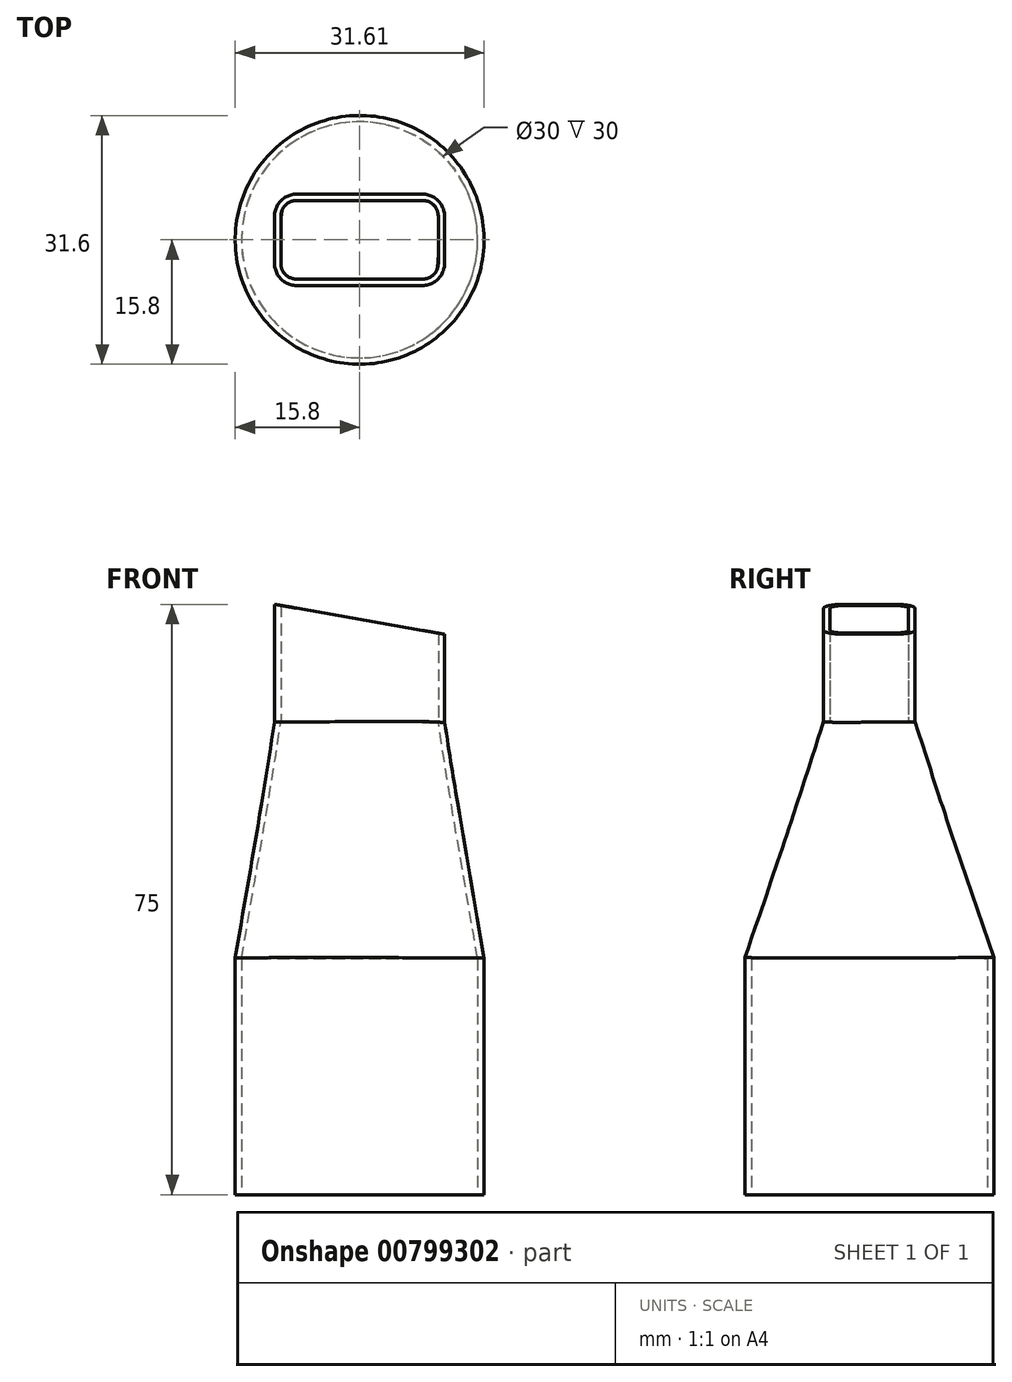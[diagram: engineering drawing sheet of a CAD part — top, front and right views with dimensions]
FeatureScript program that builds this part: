
annotation { "Feature Type Name" : "Feature", "Feature Type Description" : "" }
export const myFeature = defineFeature(function(context is Context, id is Id, definition is map)
    precondition{}
    {
        {
            var Q0;
            Q0=qCreatedBy(makeId("Top.planeOp"),FACE);
            var sketch = newSketch(context, id + "F0", { "sketchPlane" : qUnion([Q0])});
            skCircle(sketch, "E0", {"center": v(0, 0) * mm, "radius": 15 * mm});
            skSolve(sketch);
        }
        {
            var Q0;
            Q0=makeQuery(id+"F0.imprint","IMPRINT",FACE,{"disambiguationData":[TD([[makeQuery(id+"F0.imprint","IMPRINT",EDGE,{"derivedFrom":sQuery(id+"F0.wireOp",EDGE,"E0")}),1.0]])]});
            extrude(context, id + "F1", {"entities" : qUnion([Q0]), "depth" : 30 * mm, "offsetDistance" : 25 * mm});
        }
        {
            var Q0;
            Q0=makeQuery(id+"F1.opExtrude","CAP_FACE",FACE,{"disambiguationData":[OSD([sQuery(id+"F0.wireOp",EDGE,"E0")])],"isStart":false});
            cPlane(context, id + "F2", {"entities" : qUnion([Q0]), "cplaneType" : CPlaneType.OFFSET, "offset" : 30 * mm, "width" : 150 * mm, "height" : 150 * mm});
        }
        {
            var Q0;
            Q0=qCreatedBy(id+"F2.planeOp",FACE);
            var sketch = newSketch(context, id + "F3", { "sketchPlane" : qUnion([Q0])});
            skLineSegment(sketch, "E1.bottom", {"start": v(8, 5) * mm, "end": v(-8, 5) * mm});
            skLineSegment(sketch, "E1.top", {"start": v(8, -5) * mm, "end": v(-8, -5) * mm});
            skLineSegment(sketch, "E1.left", {"start": v(10, 3) * mm, "end": v(10, -3) * mm});
            skLineSegment(sketch, "E1.right", {"start": v(-10, 3) * mm, "end": v(-10, -3) * mm});
            skPoint(sketch, "E1.middle", {"position": v(0, 0) * mm});
            skPoint(sketch, "E2.visualSharp", {"position": v(10, 5) * mm});
            skArc(sketch, "E2.filletArc", {"start": v(10, 3) * mm, "mid": v(9.41, 4.41) * mm, "end": v(8, 5) * mm});
            skPoint(sketch, "E3.visualSharp", {"position": v(-10, 5) * mm});
            skArc(sketch, "E3.filletArc", {"start": v(-8, 5) * mm, "mid": v(-9.41, 4.41) * mm, "end": v(-10, 3) * mm});
            skPoint(sketch, "E4.visualSharp", {"position": v(-10, -5) * mm});
            skArc(sketch, "E4.filletArc", {"start": v(-10, -3) * mm, "mid": v(-9.41, -4.41) * mm, "end": v(-8, -5) * mm});
            skPoint(sketch, "E5.visualSharp", {"position": v(10, -5) * mm});
            skArc(sketch, "E5.filletArc", {"start": v(8, -5) * mm, "mid": v(9.41, -4.41) * mm, "end": v(10, -3) * mm});
            skSolve(sketch);
        }
        {
            var Q0;
            Q0=makeQuery(id+"F3.imprint","IMPRINT",FACE,{"disambiguationData":[TD([[makeQuery(id+"F3.imprint","IMPRINT",EDGE,{"derivedFrom":sQuery(id+"F3.wireOp",EDGE,"E1.bottom")}),1.0]])]});
            extrude(context, id + "F4", {"entities" : qUnion([Q0]), "depth" : 15 * mm, "offsetDistance" : 25 * mm});
        }
        {
            var Q1;
            Q1=makeQuery(id+"F1.opExtrude","CAP_FACE",FACE,{"disambiguationData":[OSD([sQuery(id+"F0.wireOp",EDGE,"E0")])],"isStart":false});
            var Q2;
            Q2=makeQuery(id+"F4.opExtrude","CAP_FACE",FACE,{"disambiguationData":[OSD([sQuery(id+"F3.wireOp",EDGE,"E1.bottom"),sQuery(id+"F3.wireOp",EDGE,"E1.top"),sQuery(id+"F3.wireOp",EDGE,"E1.left"),sQuery(id+"F3.wireOp",EDGE,"E1.right"),sQuery(id+"F3.wireOp",EDGE,"E2.filletArc"),sQuery(id+"F3.wireOp",EDGE,"E3.filletArc"),sQuery(id+"F3.wireOp",EDGE,"E4.filletArc"),sQuery(id+"F3.wireOp",EDGE,"E5.filletArc")])],"isStart":true});
            loft(context, id + "F5", {"operationType" : NewBodyOperationType.ADD, "sheetProfilesArray" : [{ "sheetProfileEntities" : qUnion([Q1]) }, { "sheetProfileEntities" : qUnion([Q2]) }]});
        }
        {
            var Q0;
            Q0=makeQuery(id+"F1.opExtrude","CAP_FACE",FACE,{"disambiguationData":[OSD([sQuery(id+"F0.wireOp",EDGE,"E0")])],"isStart":true});
            shell(context, id + "F6", {"entities" : qUnion([Q0]), "thickness" : 0.8 * mm, "oppositeDirection" : true});
        }
        {
            var Q0;
            Q0=makeQuery(id+"F4.opExtrude","SWEPT_FACE",FACE,{"disambiguationData":[OSD([sQuery(id+"F3.wireOp",EDGE,"E1.top")])]});
            var sketch = newSketch(context, id + "F7", { "sketchPlane" : qUnion([Q0])});
            skFitSpline(sketch, "E6.0.0", {"points": [v(-10.8, 60.06) * mm, v(-10.8, 60.05) * mm, v(-10.69, 60.04) * mm, v(-10.35, 60.04) * mm, v(-10, 60.04) * mm, v(-9.64, 60.04) * mm, v(-9.32, 60.04) * mm, v(-9.08, 60.05) * mm, v(-8.82, 60.04) * mm, v(-8.55, 60.04) * mm, v(-8.28, 60.04) * mm, v(-8.1, 60.04) * mm, v(-8, 60.04) * mm], "construction": true});
            skLineSegment(sketch, "E6.0.1", {"start": v(-8, 60.04) * mm, "end": v(-8, 75.8) * mm, "construction": true});
            skLineSegment(sketch, "E6.0.2", {"start": v(-8, 75.8) * mm, "end": v(-10.8, 75.8) * mm, "construction": true});
            skLineSegment(sketch, "E6.0.3", {"start": v(-10.8, 75.8) * mm, "end": v(-10.8, 60.06) * mm, "construction": true});
            skFitSpline(sketch, "E7.0.0", {"points": [v(8, 60.12) * mm, v(8.37, 60.1) * mm, v(9.1, 60.07) * mm, v(10.03, 60.02) * mm, v(10.65, 60) * mm, v(10.8, 59.98) * mm, v(10.8, 59.97) * mm], "construction": true});
            skLineSegment(sketch, "E7.0.1", {"start": v(10.8, 75.8) * mm, "end": v(10.8, 59.97) * mm, "construction": true});
            skLineSegment(sketch, "E7.0.2", {"start": v(10.8, 75.8) * mm, "end": v(8, 75.8) * mm, "construction": true});
            skLineSegment(sketch, "E7.0.3", {"start": v(8, 75.8) * mm, "end": v(8, 60.12) * mm, "construction": true});
            skLineSegment(sketch, "E8", {"start": v(-10.8, 75.8) * mm, "end": v(-10.8, 75) * mm});
            skLineSegment(sketch, "E9", {"start": v(-10.8, 75) * mm, "end": v(10.8, 71.2) * mm});
            skLineSegment(sketch, "E10", {"start": v(10.8, 71.2) * mm, "end": v(10.8, 75.8) * mm});
            skLineSegment(sketch, "E11", {"start": v(10.8, 75.8) * mm, "end": v(-10.8, 75.8) * mm});
            skSolve(sketch);
        }
        {
            var Q0;
            {var subQ0=sQuery(id+"F7.wireOp",EDGE,"E8");Q0=makeQuery(id+"F7.imprint","IMPRINT",FACE,{"disambiguationData":[TD([[makeQuery(id+"F7.imprint","IMPRINT",EDGE,{"derivedFrom":subQ0}),1.0]])]});}
            var Q1;
            {var subQ0=sQuery(id+"F7.wireOp",EDGE,"E9");var subQ1=sQuery(id+"F3.wireOp",EDGE,"E1.top");var subQ2=makeQuery(id+"F4.opExtrude","SWEPT_EDGE",EDGE,{"disambiguationData":[OSD([subQ1,sQuery(id+"F3.wireOp",EDGE,"E4.filletArc")])]});var subQ3=makeQuery(id+"F7.imprint","INTERSECT",VERTEX,{"derivedFrom":[subQ2,subQ0]});Q1=makeQuery(id+"F7.imprint","IMPRINT",FACE,{"disambiguationData":[TD([[makeQuery(id+"F7.imprint","IMPRINT",EDGE,{"disambiguationData":[TD([[subQ3,-1.0]])],"derivedFrom":subQ0}),1.0]])]});}
            var Q2;
            {var subQ0=sQuery(id+"F7.wireOp",EDGE,"E10");Q2=makeQuery(id+"F7.imprint","IMPRINT",FACE,{"disambiguationData":[TD([[makeQuery(id+"F7.imprint","IMPRINT",EDGE,{"derivedFrom":subQ0}),1.0]])]});}
            extrude(context, id + "F8", {"entities" : qUnion([Q0, Q1, Q2]), "operationType" : NewBodyOperationType.REMOVE, "oppositeDirection" : true, "depth" : 25 * mm, "offsetDistance" : 25 * mm});
        }
    });
